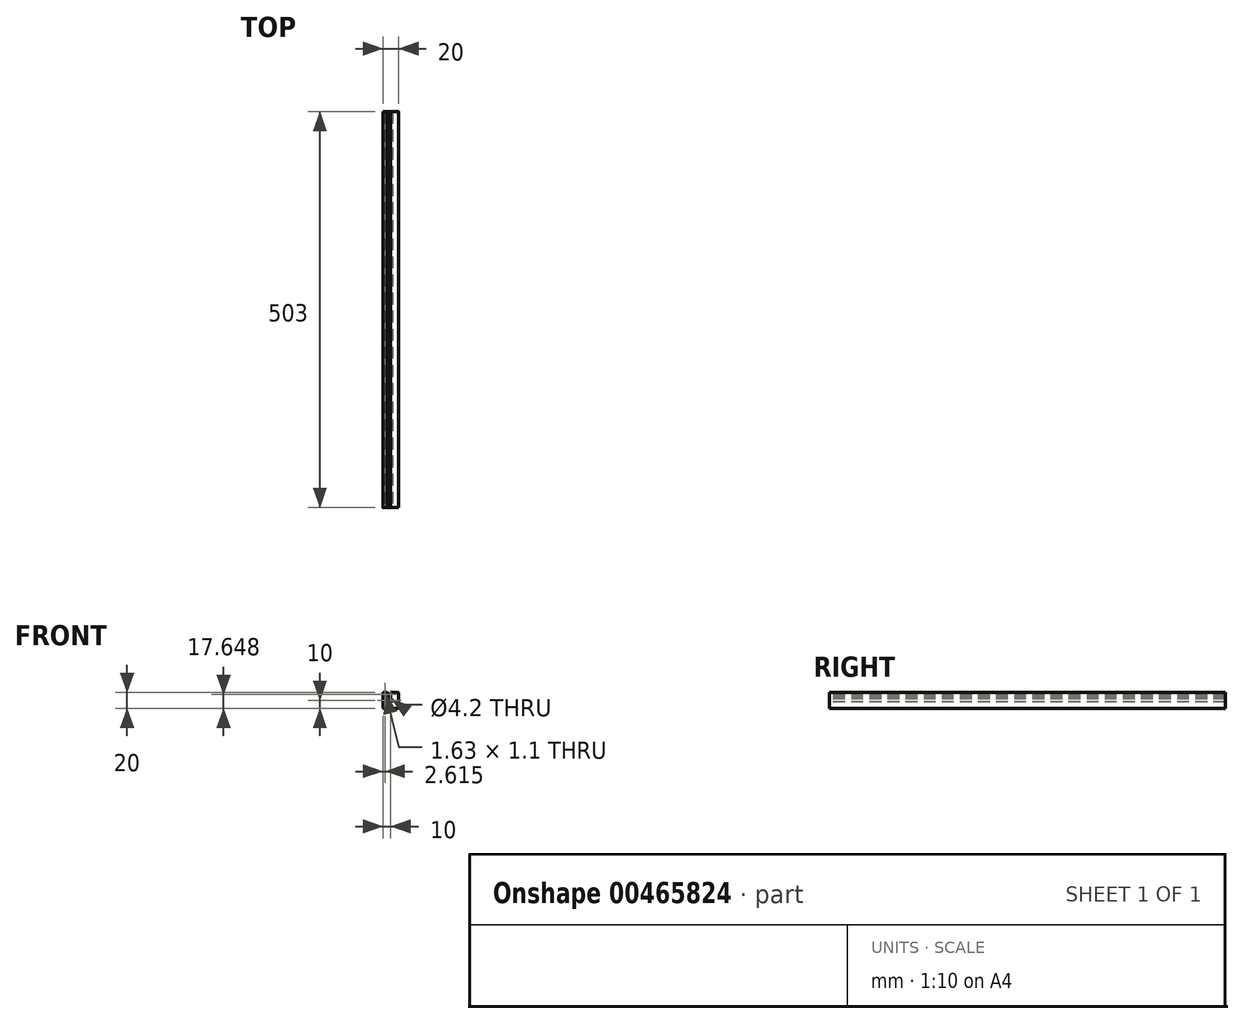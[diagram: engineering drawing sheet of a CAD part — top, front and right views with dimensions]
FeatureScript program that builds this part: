
annotation { "Feature Type Name" : "Feature", "Feature Type Description" : "" }
export const myFeature = defineFeature(function(context is Context, id is Id, definition is map)
    precondition{}
    {
        {
            var Q0;
            Q0=qCreatedBy(makeId("Front.planeOp"),FACE);
            var sketch = newSketch(context, id + "F0", { "sketchPlane" : qUnion([Q0])});
            skLineSegment(sketch, "E0.bottom", {"start": v(10, 10) * mm, "end": v(-10, 10) * mm});
            skLineSegment(sketch, "E0.top", {"start": v(10, -10) * mm, "end": v(-10, -10) * mm});
            skLineSegment(sketch, "E0.left", {"start": v(10, 10) * mm, "end": v(10, -10) * mm});
            skLineSegment(sketch, "E0.right", {"start": v(-10, 10) * mm, "end": v(-10, -10) * mm});
            skPoint(sketch, "E0.middle", {"position": v(0, 0) * mm});
            skSolve(sketch);
        }
        {
            var Q0;
            Q0=qSketchRegion(id+"F0",true);
            extrude(context, id + "F1", {"entities" : qUnion([Q0]), "depth" : 503 * mm});
        }
        {
            var Q0;
            Q0=makeQuery(id+"F1.opExtrude","CAP_FACE",FACE,{"disambiguationData":[OSD([sQuery(id+"F0.wireOp",EDGE,"E0.bottom"),sQuery(id+"F0.wireOp",EDGE,"E0.top"),sQuery(id+"F0.wireOp",EDGE,"E0.left"),sQuery(id+"F0.wireOp",EDGE,"E0.right")])],"isStart":false});
            var sketch = newSketch(context, id + "F2", { "sketchPlane" : qUnion([Q0])});
            skCircle(sketch, "E1", {"center": v(0, 0) * mm, "radius": 2.1 * mm});
            skSolve(sketch);
        }
        {
            var Q0;
            Q0=qSketchRegion(id+"F2",true);
            extrude(context, id + "F3", {"entities" : qUnion([Q0]), "operationType" : NewBodyOperationType.REMOVE, "endBound" : BoundingType.THROUGH_ALL, "oppositeDirection" : true, "depth" : 25 * mm});
        }
        {
            var Q0;
            Q0=makeQuery(id+"F1.opExtrude","SWEPT_EDGE",EDGE,{"disambiguationData":[OSD([sQuery(id+"F0.wireOp",EDGE,"E0.bottom"),sQuery(id+"F0.wireOp",EDGE,"E0.right")])]});
            var Q1;
            Q1=makeQuery(id+"F1.opExtrude","SWEPT_EDGE",EDGE,{"disambiguationData":[OSD([sQuery(id+"F0.wireOp",EDGE,"E0.bottom"),sQuery(id+"F0.wireOp",EDGE,"E0.left")])]});
            var Q2;
            Q2=makeQuery(id+"F1.opExtrude","SWEPT_EDGE",EDGE,{"disambiguationData":[OSD([sQuery(id+"F0.wireOp",EDGE,"E0.top"),sQuery(id+"F0.wireOp",EDGE,"E0.left")])]});
            var Q3;
            Q3=makeQuery(id+"F1.opExtrude","SWEPT_EDGE",EDGE,{"disambiguationData":[OSD([sQuery(id+"F0.wireOp",EDGE,"E0.top"),sQuery(id+"F0.wireOp",EDGE,"E0.right")])]});
            fillet(context, id + "F4", {"entities" : qUnion([Q0, Q1, Q2, Q3]), "radius" : 1 * mm, "tangentPropagation" : true, "allowEdgeOverflow" : false});
        }
        {
            var Q0;
            Q0=makeQuery(id+"F1.opExtrude","CAP_FACE",FACE,{"disambiguationData":[OSD([sQuery(id+"F0.wireOp",EDGE,"E0.bottom"),sQuery(id+"F0.wireOp",EDGE,"E0.top"),sQuery(id+"F0.wireOp",EDGE,"E0.left"),sQuery(id+"F0.wireOp",EDGE,"E0.right")])],"isStart":false});
            var sketch = newSketch(context, id + "F5", { "sketchPlane" : qUnion([Q0])});
            skLineSegment(sketch, "E2", {"start": v(0, 10) * mm, "end": v(-2.84, 10) * mm});
            skLineSegment(sketch, "E3", {"start": v(-2.84, 10) * mm, "end": v(-2.84, 8.2) * mm, "construction": true});
            skLineSegment(sketch, "E4", {"start": v(-2.84, 8.2) * mm, "end": v(-5.5, 8.2) * mm});
            skLineSegment(sketch, "E5", {"start": v(-2.84, 3.9) * mm, "end": v(0, 3.9) * mm});
            skLineSegment(sketch, "E6", {"start": v(0, 3.9) * mm, "end": v(0, 10) * mm});
            skLineSegment(sketch, "E7", {"start": v(-5.5, 8.2) * mm, "end": v(-5.5, 6.56) * mm});
            skLineSegment(sketch, "E8", {"start": v(-5.5, 6.56) * mm, "end": v(-2.84, 3.9) * mm});
            skPoint(sketch, "E9.endSnap0", {"position": v(-1.42, 3.9) * mm});
            skLineSegment(sketch, "E10", {"start": v(0, 0) * mm, "end": v(-9.7, 9.7) * mm, "construction": true});
            skLineSegment(sketch, "E11", {"start": v(-2.84, 8.2) * mm, "end": v(-4.64, 10) * mm});
            skLineSegment(sketch, "E12", {"start": v(-4.64, 10) * mm, "end": v(-2.84, 10) * mm});
            skLineSegment(sketch, "E13", {"start": v(-8.2, 8.2) * mm, "end": v(-6.57, 8.2) * mm});
            skLineSegment(sketch, "E14", {"start": v(-6.57, 8.2) * mm, "end": v(-6.57, 7.62) * mm});
            skLineSegment(sketch, "E15", {"start": v(-6.57, 7.62) * mm, "end": v(-7.1, 7.1) * mm});
            skLineSegment(sketch, "E16", {"start": v(-7.1, 7.1) * mm, "end": v(-8.2, 8.2) * mm});
            skSolve(sketch);
        }
        {
            var Q0;
            Q0=qSketchRegion(id+"F5",true);
            extrude(context, id + "F6", {"entities" : qUnion([Q0]), "operationType" : NewBodyOperationType.REMOVE, "endBound" : BoundingType.THROUGH_ALL, "oppositeDirection" : true, "depth" : 25 * mm});
        }
        {
            var Q0;
            Q0=qCreatedBy(makeId("Top.planeOp"),FACE);
            var sketch = newSketch(context, id + "F7", { "sketchPlane" : qUnion([Q0])});
            skLineSegment(sketch, "E17", {"start": v(0, 0) * mm, "end": v(0, -25.58) * mm, "construction": true});
            skSolve(sketch);
        }
    });
